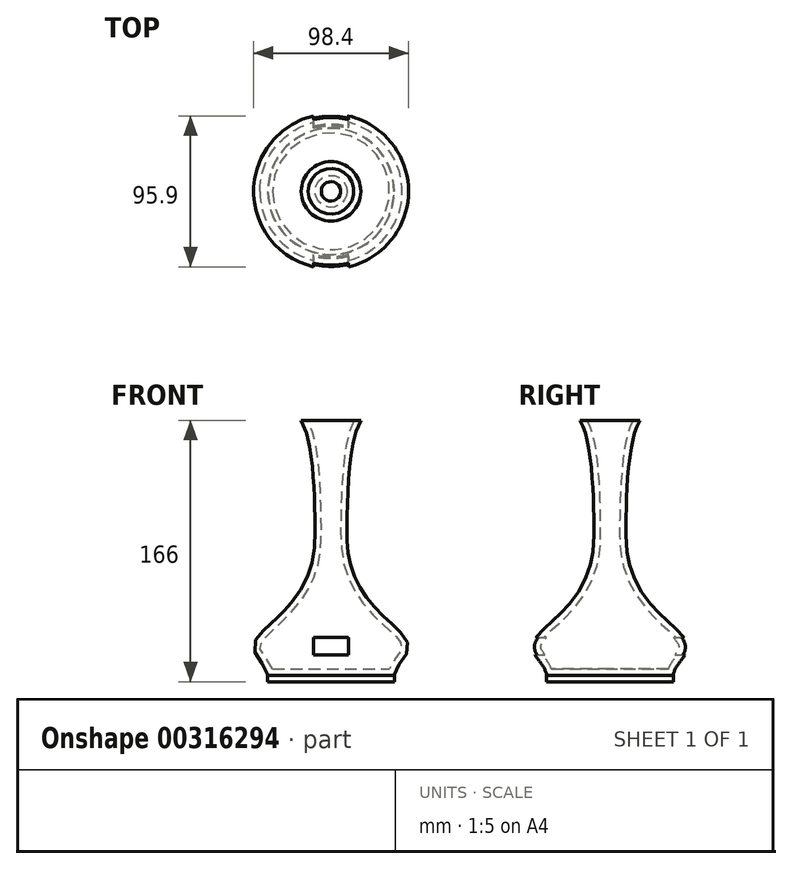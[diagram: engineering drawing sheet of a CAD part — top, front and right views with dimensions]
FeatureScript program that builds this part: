
annotation { "Feature Type Name" : "Feature", "Feature Type Description" : "" }
export const myFeature = defineFeature(function(context is Context, id is Id, definition is map)
    precondition{}
    {
        {
            var Q0;
            Q0=qCreatedBy(makeId("Top.planeOp"),FACE);
            var sketch = newSketch(context, id + "F0", { "sketchPlane" : qUnion([Q0])});
            skCircle(sketch, "E0", {"center": v(0, 0) * mm, "radius": 40 * mm});
            skSolve(sketch);
        }
        {
            var Q0;
            Q0=makeQuery(id+"F0.imprint","IMPRINT",FACE,{"disambiguationData":[TD([[makeQuery(id+"F0.imprint","IMPRINT",EDGE,{"derivedFrom":sQuery(id+"F0.wireOp",EDGE,"E0")}),1.0]])]});
            cPlane(context, id + "F1", {"entities" : qUnion([Q0]), "cplaneType" : CPlaneType.OFFSET, "offset" : 4 * mm, "width" : 150 * mm, "height" : 150 * mm});
        }
        {
            var Q0;
            Q0=qCreatedBy(id+"F1.planeOp",FACE);
            var sketch = newSketch(context, id + "F2", { "sketchPlane" : qUnion([Q0])});
            skCircle(sketch, "E1", {"center": v(0, 0) * mm, "radius": 41.51 * mm});
            skSolve(sketch);
        }
        {
            var Q0;
            Q0=makeQuery(id+"F2.imprint","IMPRINT",FACE,{"disambiguationData":[TD([[makeQuery(id+"F2.imprint","IMPRINT",EDGE,{"derivedFrom":sQuery(id+"F2.wireOp",EDGE,"E1")}),1.0]])]});
            cPlane(context, id + "F3", {"entities" : qUnion([Q0]), "cplaneType" : CPlaneType.OFFSET, "offset" : 6 * mm, "width" : 150 * mm, "height" : 150 * mm});
        }
        {
            var Q0;
            Q0=qCreatedBy(id+"F3.planeOp",FACE);
            var sketch = newSketch(context, id + "F4", { "sketchPlane" : qUnion([Q0])});
            skCircle(sketch, "E2", {"center": v(0, 0) * mm, "radius": 45.5 * mm});
            skSolve(sketch);
        }
        {
            var Q0;
            Q0=makeQuery(id+"F4.imprint","IMPRINT",FACE,{"disambiguationData":[TD([[makeQuery(id+"F4.imprint","IMPRINT",EDGE,{"derivedFrom":sQuery(id+"F4.wireOp",EDGE,"E2")}),1.0]])]});
            cPlane(context, id + "F5", {"entities" : qUnion([Q0]), "cplaneType" : CPlaneType.OFFSET, "offset" : 8 * mm, "width" : 150 * mm, "height" : 150 * mm});
        }
        {
            var Q0;
            Q0=qCreatedBy(id+"F5.planeOp",FACE);
            var sketch = newSketch(context, id + "F6", { "sketchPlane" : qUnion([Q0])});
            skCircle(sketch, "E3", {"center": v(0, 0) * mm, "radius": 49.2 * mm});
            skSolve(sketch);
        }
        {
            var Q0;
            Q0=makeQuery(id+"F6.imprint","IMPRINT",FACE,{"disambiguationData":[TD([[makeQuery(id+"F6.imprint","IMPRINT",EDGE,{"derivedFrom":sQuery(id+"F6.wireOp",EDGE,"E3")}),1.0]])]});
            cPlane(context, id + "F7", {"entities" : qUnion([Q0]), "cplaneType" : CPlaneType.OFFSET, "offset" : 6 * mm, "width" : 150 * mm, "height" : 150 * mm});
        }
        {
            var Q0;
            Q0=qCreatedBy(id+"F7.planeOp",FACE);
            var sketch = newSketch(context, id + "F8", { "sketchPlane" : qUnion([Q0])});
            skCircle(sketch, "E4", {"center": v(0, 0) * mm, "radius": 47 * mm});
            skSolve(sketch);
        }
        {
            var Q0;
            Q0=qCreatedBy(id+"F7.planeOp",FACE);
            cPlane(context, id + "F9", {"entities" : qUnion([Q0]), "cplaneType" : CPlaneType.OFFSET, "offset" : 6 * mm, "width" : 150 * mm, "height" : 150 * mm});
        }
        {
            var Q0;
            Q0=qCreatedBy(id+"F9.planeOp",FACE);
            var sketch = newSketch(context, id + "F10", { "sketchPlane" : qUnion([Q0])});
            skCircle(sketch, "E5", {"center": v(0, 0) * mm, "radius": 41.44 * mm});
            skSolve(sketch);
        }
        {
            var Q0;
            Q0=qCreatedBy(id+"F9.planeOp",FACE);
            cPlane(context, id + "F11", {"entities" : qUnion([Q0]), "cplaneType" : CPlaneType.OFFSET, "offset" : 16 * mm, "width" : 150 * mm, "height" : 150 * mm});
        }
        {
            var Q0;
            Q0=qCreatedBy(id+"F11.planeOp",FACE);
            var sketch = newSketch(context, id + "F12", { "sketchPlane" : qUnion([Q0])});
            skCircle(sketch, "E6", {"center": v(0, 0) * mm, "radius": 25.29 * mm});
            skSolve(sketch);
        }
        {
            var Q0;
            Q0=qCreatedBy(id+"F11.planeOp",FACE);
            cPlane(context, id + "F13", {"entities" : qUnion([Q0]), "cplaneType" : CPlaneType.OFFSET, "offset" : 25 * mm, "width" : 150 * mm, "height" : 150 * mm});
        }
        {
            var Q0;
            Q0=qCreatedBy(id+"F13.planeOp",FACE);
            var sketch = newSketch(context, id + "F14", { "sketchPlane" : qUnion([Q0])});
            skCircle(sketch, "E7", {"center": v(0, 0) * mm, "radius": 12.22 * mm});
            skSolve(sketch);
        }
        {
            var Q0;
            Q0=qCreatedBy(id+"F13.planeOp",FACE);
            cPlane(context, id + "F15", {"entities" : qUnion([Q0]), "cplaneType" : CPlaneType.OFFSET, "offset" : 25 * mm, "width" : 150 * mm, "height" : 150 * mm});
        }
        {
            var Q0;
            Q0=qCreatedBy(id+"F15.planeOp",FACE);
            var sketch = newSketch(context, id + "F16", { "sketchPlane" : qUnion([Q0])});
            skCircle(sketch, "E8", {"center": v(0, 0) * mm, "radius": 10.18 * mm});
            skSolve(sketch);
        }
        {
            var Q0;
            Q0=qCreatedBy(id+"F15.planeOp",FACE);
            cPlane(context, id + "F17", {"entities" : qUnion([Q0]), "cplaneType" : CPlaneType.OFFSET, "offset" : 25 * mm, "width" : 150 * mm, "height" : 150 * mm});
        }
        {
            var Q0;
            Q0=qCreatedBy(id+"F17.planeOp",FACE);
            var sketch = newSketch(context, id + "F18", { "sketchPlane" : qUnion([Q0])});
            skCircle(sketch, "E9", {"center": v(0, 0) * mm, "radius": 11 * mm});
            skSolve(sketch);
        }
        {
            var Q0;
            Q0=qCreatedBy(id+"F17.planeOp",FACE);
            cPlane(context, id + "F19", {"entities" : qUnion([Q0]), "cplaneType" : CPlaneType.OFFSET, "offset" : 25 * mm, "width" : 150 * mm, "height" : 150 * mm});
        }
        {
            var Q0;
            Q0=qCreatedBy(id+"F19.planeOp",FACE);
            var sketch = newSketch(context, id + "F20", { "sketchPlane" : qUnion([Q0])});
            skCircle(sketch, "E10", {"center": v(0, 0) * mm, "radius": 13.75 * mm});
            skSolve(sketch);
        }
        {
            var Q0;
            Q0=qCreatedBy(id+"F19.planeOp",FACE);
            cPlane(context, id + "F21", {"entities" : qUnion([Q0]), "cplaneType" : CPlaneType.OFFSET, "offset" : 10 * mm, "width" : 150 * mm, "height" : 150 * mm});
        }
        {
            var Q0;
            Q0=qCreatedBy(id+"F21.planeOp",FACE);
            var sketch = newSketch(context, id + "F22", { "sketchPlane" : qUnion([Q0])});
            skCircle(sketch, "E11", {"center": v(0, 0) * mm, "radius": 16.33 * mm});
            skSolve(sketch);
        }
        {
            var Q0;
            Q0=qCreatedBy(id+"F21.planeOp",FACE);
            cPlane(context, id + "F23", {"entities" : qUnion([Q0]), "cplaneType" : CPlaneType.OFFSET, "offset" : 6 * mm, "width" : 150 * mm, "height" : 150 * mm});
        }
        {
            var Q0;
            Q0=qCreatedBy(id+"F23.planeOp",FACE);
            var sketch = newSketch(context, id + "F24", { "sketchPlane" : qUnion([Q0])});
            skCircle(sketch, "E12", {"center": v(0, 0) * mm, "radius": 18.94 * mm});
            skSolve(sketch);
        }
        {
            var Q0;
            Q0=qSketchRegion(id+"F0",true);
            var Q1;
            Q1=qSketchRegion(id+"F2",true);
            var Q2;
            Q2=qSketchRegion(id+"F4",true);
            var Q3;
            Q3=qSketchRegion(id+"F6",true);
            var Q4;
            Q4=qSketchRegion(id+"F8",true);
            var Q5;
            Q5=qSketchRegion(id+"F10",true);
            var Q6;
            Q6=qSketchRegion(id+"F12",true);
            var Q7;
            Q7=qSketchRegion(id+"F14",true);
            var Q8;
            Q8=qSketchRegion(id+"F16",true);
            var Q9;
            Q9=qSketchRegion(id+"F18",true);
            var Q10;
            Q10=qSketchRegion(id+"F20",true);
            var Q11;
            Q11=qSketchRegion(id+"F22",true);
            var Q12;
            Q12=qSketchRegion(id+"F24",true);
            loft(context, id + "F25", {"sheetProfilesArray" : [{ "sheetProfileEntities" : qUnion([Q0]) }, { "sheetProfileEntities" : qUnion([Q1]) }, { "sheetProfileEntities" : qUnion([Q2]) }, { "sheetProfileEntities" : qUnion([Q3]) }, { "sheetProfileEntities" : qUnion([Q4]) }, { "sheetProfileEntities" : qUnion([Q5]) }, { "sheetProfileEntities" : qUnion([Q6]) }, { "sheetProfileEntities" : qUnion([Q7]) }, { "sheetProfileEntities" : qUnion([Q8]) }, { "sheetProfileEntities" : qUnion([Q9]) }, { "sheetProfileEntities" : qUnion([Q10]) }, { "sheetProfileEntities" : qUnion([Q11]) }, { "sheetProfileEntities" : qUnion([Q12]) }]});
        }
        {
            var Q0;
            Q0=makeQuery(id+"F25.opLoft","CAP_FACE",FACE,{"disambiguationData":[OSD([makeQuery(id+"F24.imprint","IMPRINT",FACE,{"disambiguationData":[TD([[makeQuery(id+"F24.imprint","IMPRINT",EDGE,{"derivedFrom":sQuery(id+"F24.wireOp",EDGE,"E12")}),1.0]])]})])],"isStart":true});
            shell(context, id + "F26", {"entities" : qUnion([Q0]), "thickness" : 4 * mm});
        }
        {
            var Q0;
            Q0=qCreatedBy(makeId("Top.planeOp"),FACE);
            var sketch = newSketch(context, id + "F27", { "sketchPlane" : qUnion([Q0])});
            skCircle(sketch, "E13", {"center": v(0, 0) * mm, "radius": 40.24 * mm});
            skSolve(sketch);
        }
        {
            var Q0;
            Q0=qSketchRegion(id+"F27",true);
            extrude(context, id + "F28", {"entities" : qUnion([Q0]), "operationType" : NewBodyOperationType.ADD, "oppositeDirection" : true, "depth" : 4 * mm});
        }
        {
            var Q0;
            Q0=qCreatedBy(makeId("Front.planeOp"),FACE);
            var sketch = newSketch(context, id + "F29", { "sketchPlane" : qUnion([Q0])});
            skLineSegment(sketch, "E14.bottom", {"start": v(-11, 24.14) * mm, "end": v(11, 24.14) * mm});
            skLineSegment(sketch, "E14.top", {"start": v(-11, 13.14) * mm, "end": v(11, 13.14) * mm});
            skLineSegment(sketch, "E14.left", {"start": v(-11, 24.14) * mm, "end": v(-11, 13.14) * mm});
            skLineSegment(sketch, "E14.right", {"start": v(11, 24.14) * mm, "end": v(11, 13.14) * mm});
            skLineSegment(sketch, "E15", {"start": v(0, 0) * mm, "end": v(0, 98.34) * mm, "construction": true});
            skSolve(sketch);
        }
        {
            var Q0;
            Q0=qSketchRegion(id+"F29",true);
            extrude(context, id + "F30", {"entities" : qUnion([Q0]), "operationType" : NewBodyOperationType.REMOVE, "endBound" : BoundingType.SYMMETRIC, "depth" : 144 * mm, "offsetDistance" : 25 * mm});
        }
    });
